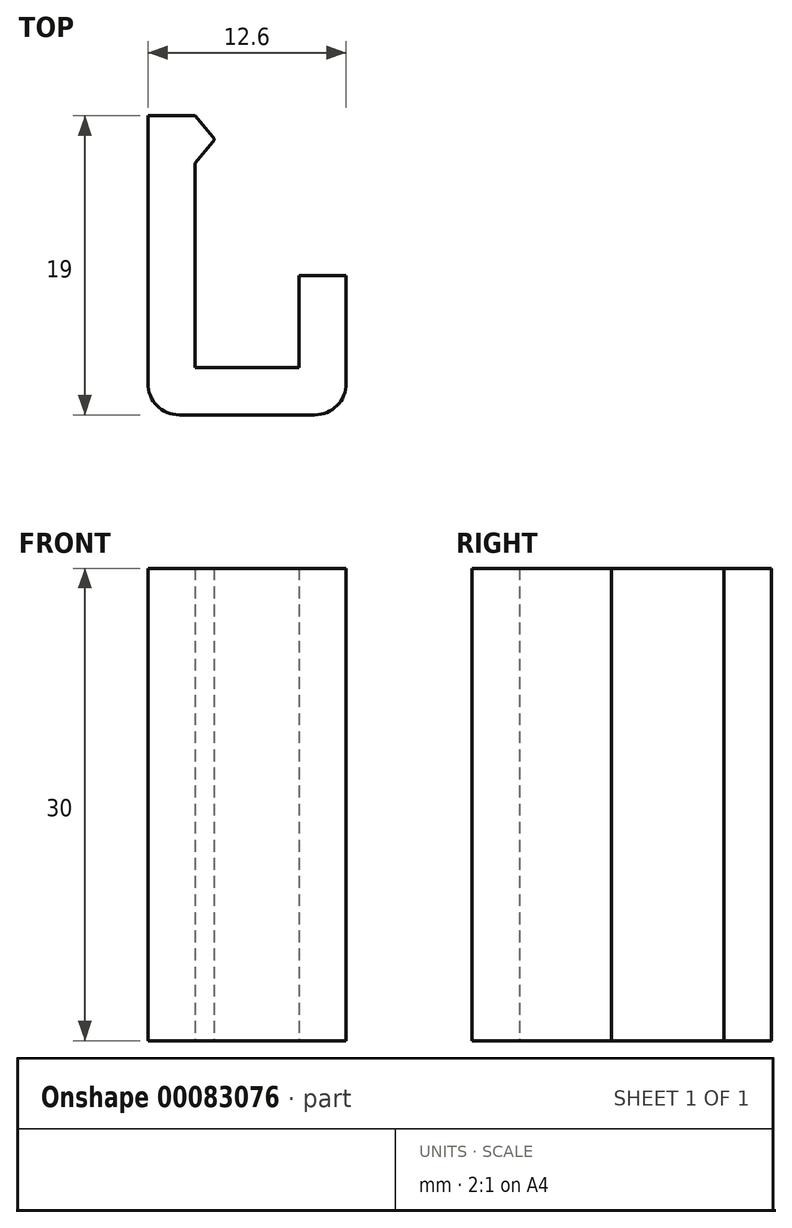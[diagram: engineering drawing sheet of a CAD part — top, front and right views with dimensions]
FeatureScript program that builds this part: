
annotation { "Feature Type Name" : "Feature", "Feature Type Description" : "" }
export const myFeature = defineFeature(function(context is Context, id is Id, definition is map)
    precondition{}
    {
        {
            var Q0;
            Q0=qCreatedBy(makeId("Top.planeOp"),FACE);
            var sketch = newSketch(context, id + "F0", { "sketchPlane" : qUnion([Q0])});
            skLineSegment(sketch, "E0", {"start": v(-12.6, 19) * mm, "end": v(-12.6, 2) * mm});
            skLineSegment(sketch, "E1", {"start": v(-10.6, 0) * mm, "end": v(-2, 0) * mm});
            skLineSegment(sketch, "E2", {"start": v(0, 2) * mm, "end": v(0, 8.85) * mm});
            skLineSegment(sketch, "E3.0", {"start": v(-3, 3) * mm, "end": v(-3, 8.85) * mm});
            skLineSegment(sketch, "E3.1", {"start": v(-9.6, 3) * mm, "end": v(-3, 3) * mm});
            skLineSegment(sketch, "E3.2", {"start": v(-9.6, 16) * mm, "end": v(-9.6, 3) * mm});
            skLineSegment(sketch, "E4", {"start": v(-3, 8.85) * mm, "end": v(0, 8.85) * mm});
            skLineSegment(sketch, "E5", {"start": v(-9.6, 19) * mm, "end": v(-8.45, 17.63) * mm});
            skLineSegment(sketch, "E6", {"start": v(-8.45, 17.37) * mm, "end": v(-9.6, 16) * mm});
            skPoint(sketch, "E7.visualSharp", {"position": v(-8.34, 17.5) * mm});
            skArc(sketch, "E7.filletArc", {"start": v(-8.45, 17.37) * mm, "mid": v(-8.4, 17.5) * mm, "end": v(-8.45, 17.63) * mm});
            skLineSegment(sketch, "E8", {"start": v(-8.4, 29.06) * mm, "end": v(-8.4, 27.06) * mm, "construction": true});
            skLineSegment(sketch, "E9", {"start": v(-12.6, 19) * mm, "end": v(-9.6, 19) * mm});
            skPoint(sketch, "E10.visualSharp", {"position": v(-12.6, 0) * mm});
            skArc(sketch, "E10.filletArc", {"start": v(-12.6, 2) * mm, "mid": v(-12.01, 0.59) * mm, "end": v(-10.6, 0) * mm});
            skPoint(sketch, "E11.visualSharp", {"position": v(0, 0) * mm});
            skArc(sketch, "E11.filletArc", {"start": v(-2, 0) * mm, "mid": v(-0.59, 0.59) * mm, "end": v(0, 2) * mm});
            skSolve(sketch);
        }
        {
            var Q0;
            Q0 = qSketchRegion(id + "F0", true);
            extrude(context, id + "F1", {"entities" : qUnion([Q0]), "depth" : 30 * mm});
        }
    });
